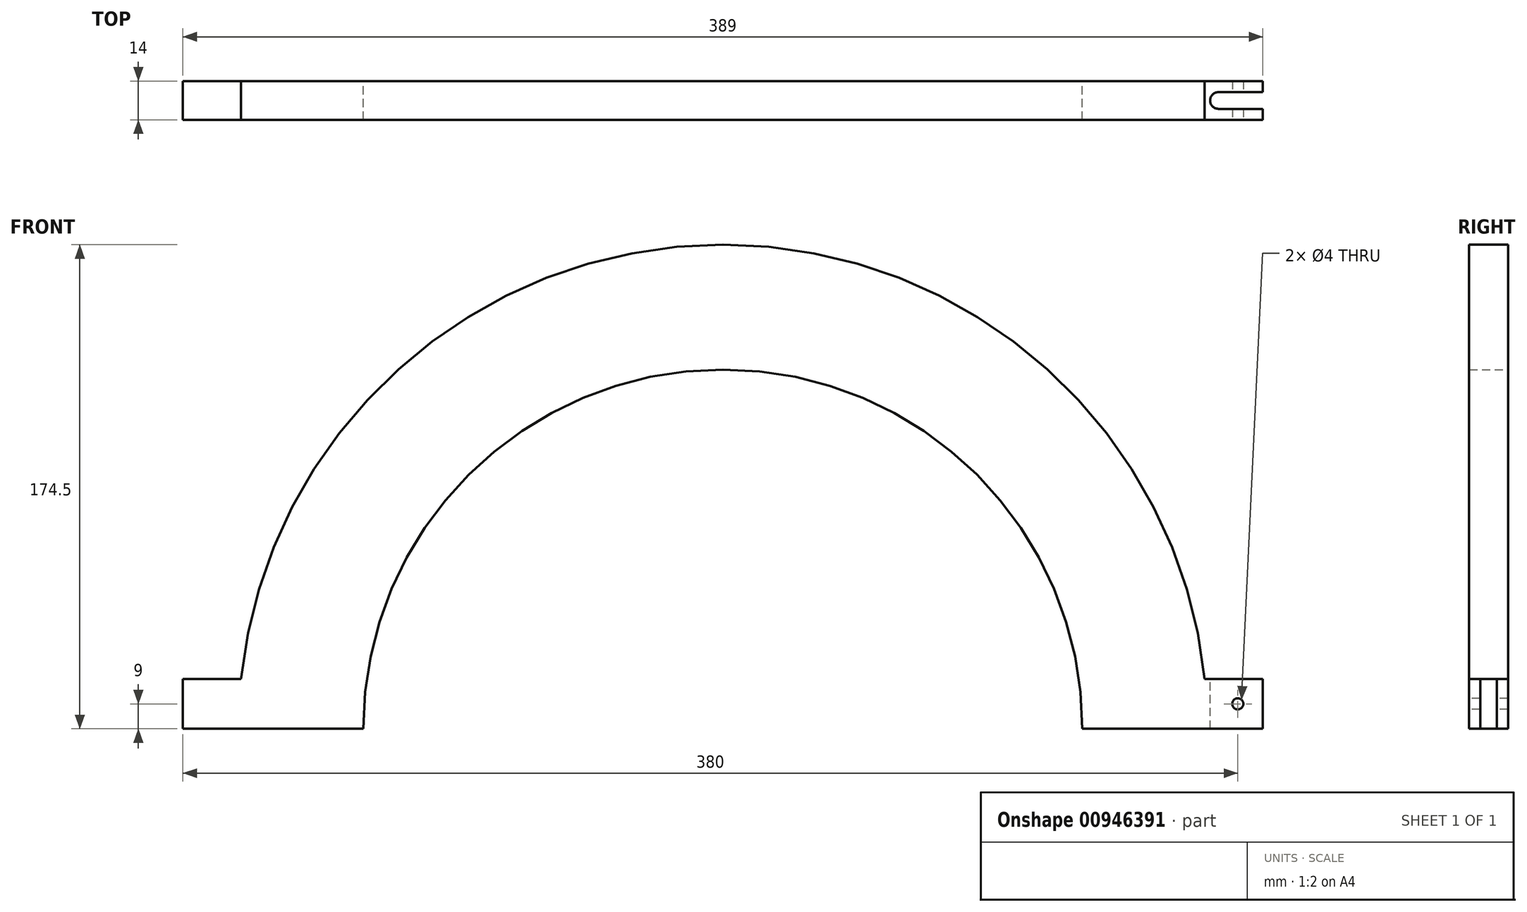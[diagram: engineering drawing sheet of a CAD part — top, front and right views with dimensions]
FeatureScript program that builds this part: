
annotation { "Feature Type Name" : "Feature", "Feature Type Description" : "" }
export const myFeature = defineFeature(function(context is Context, id is Id, definition is map)
    precondition{}
    {
        {
            var Q0;
            Q0=qCreatedBy(makeId("Front.planeOp"),FACE);
            var sketch = newSketch(context, id + "F0", { "sketchPlane" : qUnion([Q0])});
            skArc(sketch, "E0", {"start": v(174.5, 0) * mm, "mid": v(0, 174.5) * mm, "end": v(-174.5, 0) * mm});
            skArc(sketch, "E1", {"start": v(129.5, 0) * mm, "mid": v(0, 129.5) * mm, "end": v(-129.5, 0) * mm});
            skLineSegment(sketch, "E2", {"start": v(-174.5, 0) * mm, "end": v(-129.5, 0) * mm});
            skLineSegment(sketch, "E3.trimOffspring", {"start": v(129.5, 0) * mm, "end": v(174.5, 0) * mm});
            skLineSegment(sketch, "E4", {"start": v(-174.5, 0) * mm, "end": v(-174.5, -52.73) * mm, "construction": true});
            skLineSegment(sketch, "E5", {"start": v(0, 82.24) * mm, "end": v(0, -91.49) * mm, "construction": true});
            skLineSegment(sketch, "E6", {"start": v(174.5, 0) * mm, "end": v(194.5, 0) * mm});
            skLineSegment(sketch, "E7", {"start": v(194.5, 0) * mm, "end": v(194.5, 18) * mm});
            skLineSegment(sketch, "E8", {"start": v(194.5, 18) * mm, "end": v(173.57, 18) * mm});
            skLineSegment(sketch, "E9.MirrorCS", {"start": v(-194.5, 18) * mm, "end": v(-173.57, 18) * mm});
            skLineSegment(sketch, "E10.MirrorCS", {"start": v(-194.5, 0) * mm, "end": v(-194.5, 18) * mm});
            skLineSegment(sketch, "E11.MirrorCS", {"start": v(-174.5, 0) * mm, "end": v(-194.5, 0) * mm});
            skSolve(sketch);
        }
        {
            var Q0;
            Q0=qSketchRegion(id+"F0",true);
            extrude(context, id + "F1", {"entities" : qUnion([Q0]), "endBound" : BoundingType.SYMMETRIC, "depth" : 14 * mm, "offsetDistance" : 25 * mm});
        }
        {
            var Q0;
            Q0=qSketchRegion(id+"F0",true);
            extrude(context, id + "F2", {"entities" : qUnion([Q0]), "operationType" : NewBodyOperationType.ADD, "endBound" : BoundingType.SYMMETRIC, "depth" : 12 * mm, "offsetDistance" : 25 * mm});
        }
        {
            var Q0;
            Q0=makeQuery(id+"F1.opExtrude","CAP_FACE",FACE,{"disambiguationData":[OSD([sQuery(id+"F0.wireOp",EDGE,"E0"),sQuery(id+"F0.wireOp",EDGE,"E1"),sQuery(id+"F0.wireOp",EDGE,"E2"),sQuery(id+"F0.wireOp",EDGE,"E3.trimOffspring"),sQuery(id+"F0.wireOp",EDGE,"E6"),sQuery(id+"F0.wireOp",EDGE,"E7"),sQuery(id+"F0.wireOp",EDGE,"E8"),sQuery(id+"F0.wireOp",EDGE,"E9.MirrorCS"),sQuery(id+"F0.wireOp",EDGE,"E10.MirrorCS"),sQuery(id+"F0.wireOp",EDGE,"E11.MirrorCS")])],"isStart":false});
            var sketch = newSketch(context, id + "F3", { "sketchPlane" : qUnion([Q0])});
            skCircle(sketch, "E12", {"center": v(185.5, 9) * mm, "radius": 2 * mm});
            skSolve(sketch);
        }
        {
            var Q0;
            Q0=qSketchRegion(id+"F3",true);
            extrude(context, id + "F4", {"entities" : qUnion([Q0]), "operationType" : NewBodyOperationType.REMOVE, "oppositeDirection" : true, "depth" : 25 * mm, "offsetDistance" : 25 * mm});
        }
        {
            var Q0;
            Q0=makeQuery(id+"F1.opExtrude","SWEPT_FACE",FACE,{"disambiguationData":[OSD([sQuery(id+"F0.wireOp",EDGE,"E8")])]});
            var sketch = newSketch(context, id + "F5", { "sketchPlane" : qUnion([Q0])});
            skArc(sketch, "E13", {"start": v(178.5, 3) * mm, "mid": v(175.5, 0) * mm, "end": v(178.5, -3) * mm});
            skLineSegment(sketch, "E14", {"start": v(178.5, 3) * mm, "end": v(194.5, 3) * mm});
            skLineSegment(sketch, "E15", {"start": v(178.5, -3) * mm, "end": v(194.5, -3) * mm});
            skLineSegment(sketch, "E16", {"start": v(194.5, -3) * mm, "end": v(194.5, 3) * mm});
            skSolve(sketch);
        }
        {
            var Q0;
            Q0=qSketchRegion(id+"F5",true);
            extrude(context, id + "F6", {"entities" : qUnion([Q0]), "operationType" : NewBodyOperationType.REMOVE, "oppositeDirection" : true, "depth" : 25 * mm, "offsetDistance" : 25 * mm});
        }
    });
